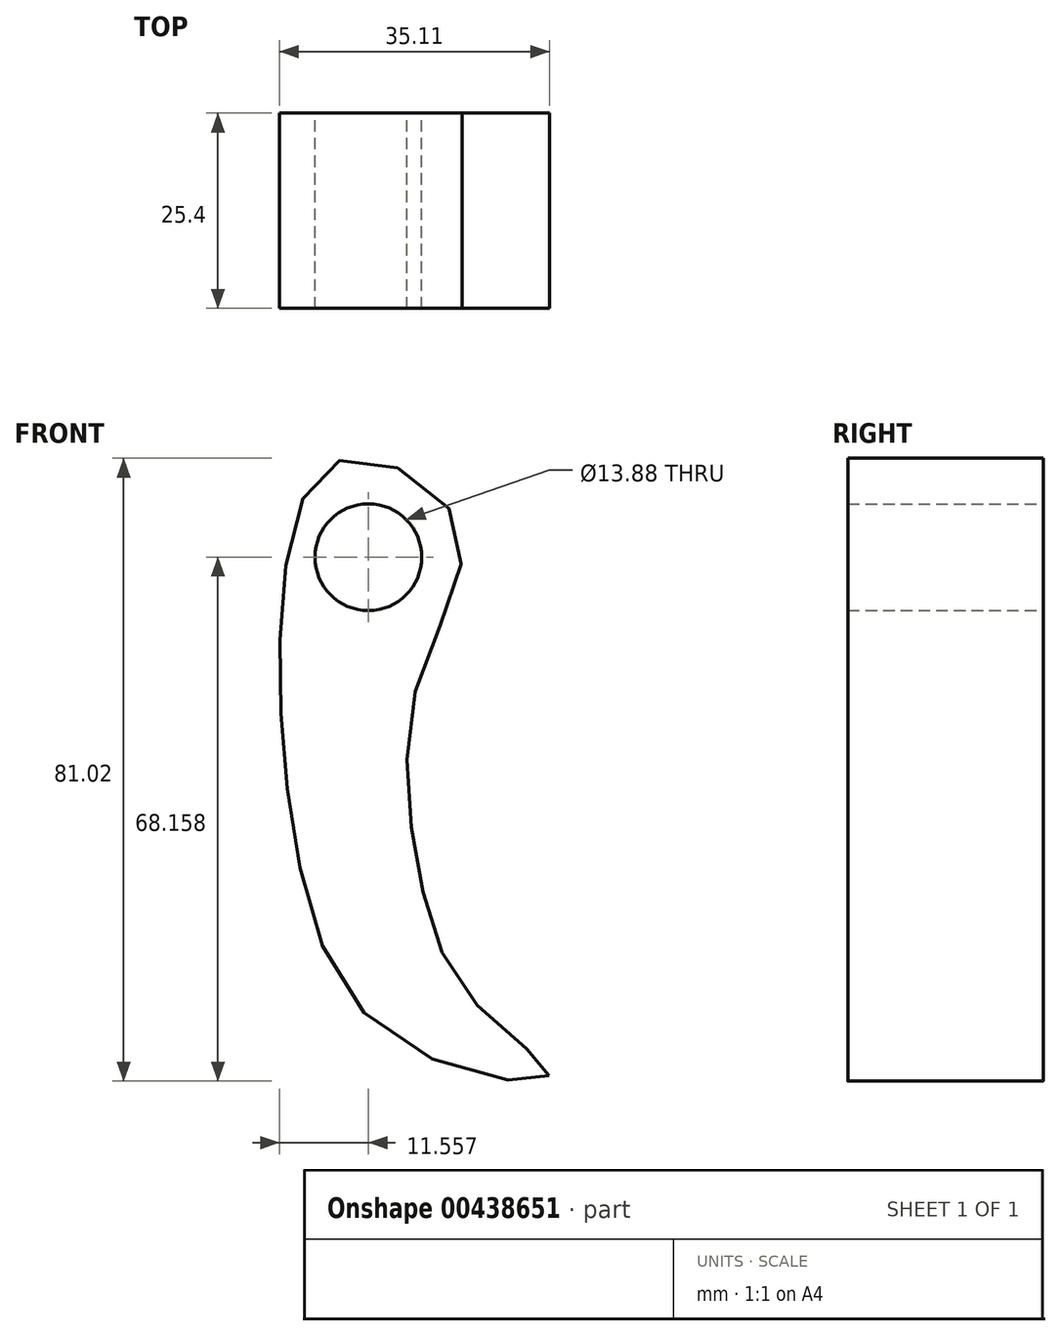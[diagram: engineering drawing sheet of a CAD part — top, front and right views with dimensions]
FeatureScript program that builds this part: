
annotation { "Feature Type Name" : "Feature", "Feature Type Description" : "" }
export const myFeature = defineFeature(function(context is Context, id is Id, definition is map)
    precondition{}
    {
        {
            var Q0;
            Q0=qCreatedBy(makeId("Front.planeOp"),FACE);
            var sketch = newSketch(context, id + "F0", { "sketchPlane" : qUnion([Q0])});
            skCircle(sketch, "E0", {"center": v(0, 0) * mm, "radius": 19 * mm});
            skFitSpline(sketch, "E1", {"points": [v(-11.86, -19.07) * mm, v(-32.1, -14.19) * mm, v(-45.35, 14.42) * mm, v(-46.52, 43.26) * mm, v(-39.07, 60.94) * mm, v(-23.72, 52.56) * mm, v(-28.84, 32.33) * mm, v(-29.07, 8.84) * mm, v(-21.17, -10) * mm, v(-11.86, -19.07) * mm]});
            skCircle(sketch, "E2", {"center": v(-35.35, 48.38) * mm, "radius": 6.94 * mm});
            skSolve(sketch);
        }
        {
            var Q0;
            Q0=makeQuery(id+"F0.imprint","IMPRINT",FACE,{"disambiguationData":[TD([[makeQuery(id+"F0.imprint","IMPRINT",EDGE,{"derivedFrom":sQuery(id+"F0.wireOp",EDGE,"E1")}),-1.0]])]});
            extrude(context, id + "F1", {"entities" : qUnion([Q0]), "depth" : 25.4 * mm});
        }
    });
